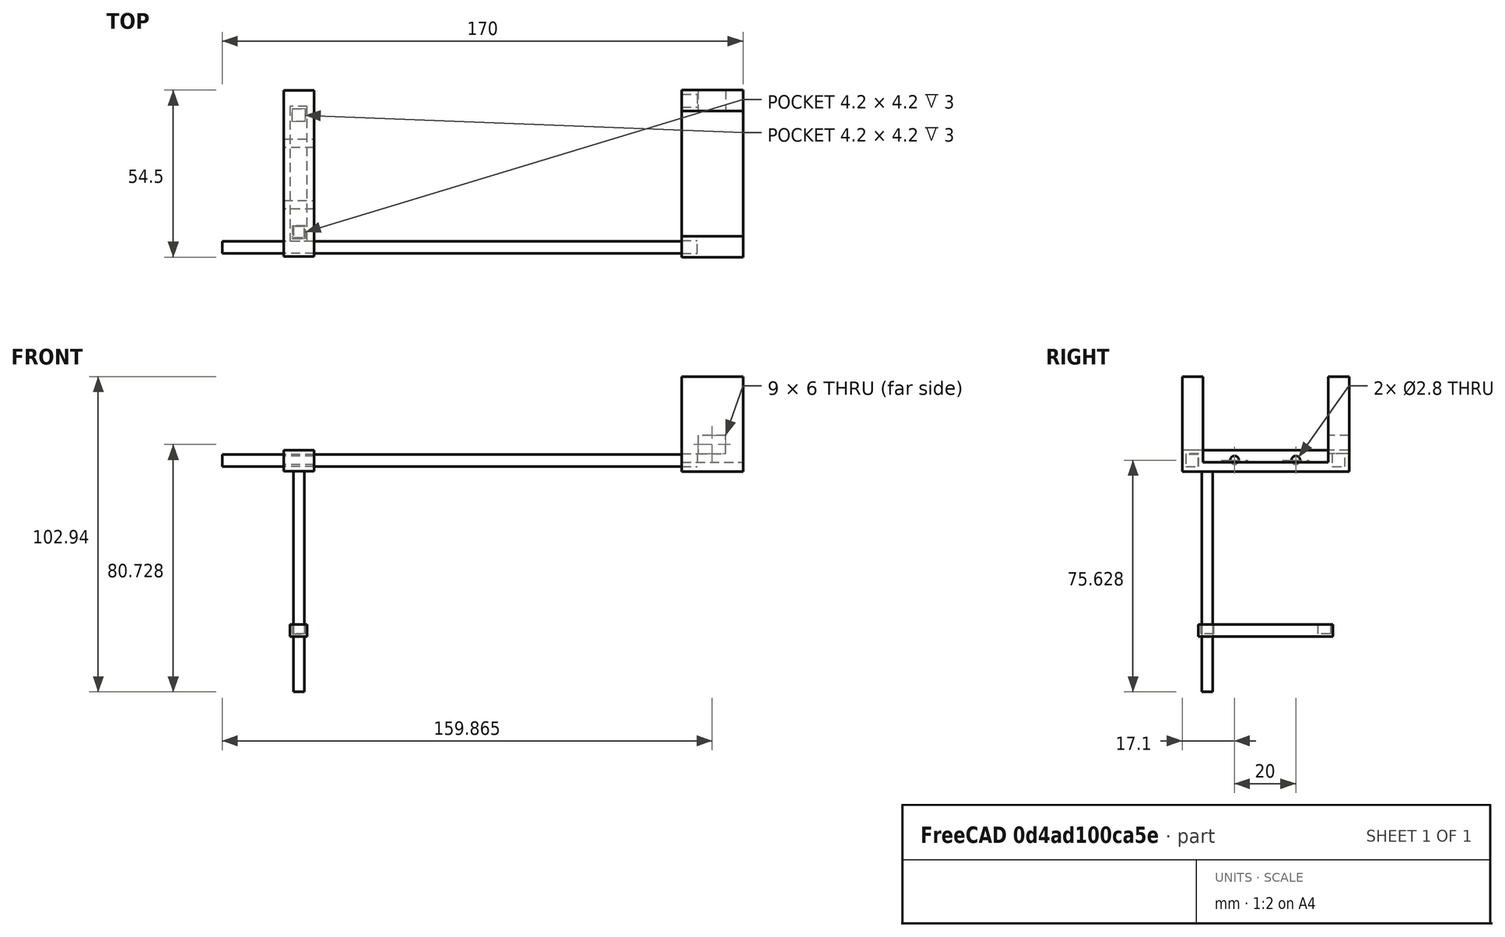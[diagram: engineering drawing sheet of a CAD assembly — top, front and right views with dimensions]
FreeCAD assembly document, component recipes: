
FREECAD ASSEMBLY — COMPONENT RECIPES ("internalstructure")

This assembly document has 7 components, labeled P0..P6 below (a component is one placed body or linked part). 7 of them carry a construction recipe — the FreeCAD feature program that regenerates the part from scratch, quoted from this document or its linked companion documents; the rest are supplied as boundary geometry only. No exploded tour is included for this assembly.
COMPONENT P0 — recipe-attached ("ServoHolderPart001", modeled in this document).
Construction recipe (the document's own serialized feature program — sketch geometry with constraints, then the solid features built on it; lengths are millimeters unless a unit is written):

FEATURE [Sketcher::SketchObject] Sketch  label="ServoHolder"
  FullyConstrained = false
  MapMode = 4
  Placement = pos=(0,0,0) rot=(0.57735,0.57735,0.57735;2.0944rad)
  sketch-geometry (8):
    g0: LineSegment StartX=-27.0989 StartY=-22.5482 StartZ=0 EndX=27.4011 EndY=-22.5482 EndZ=0
    g1: LineSegment StartX=20.6511 StartY=-19.5482 StartZ=0 EndX=20.6511 EndY=8.45178 EndZ=0
    g2: LineSegment StartX=20.6511 StartY=8.45178 StartZ=0 EndX=27.4011 EndY=8.45178 EndZ=0
    g3: LineSegment StartX=-20.3489 StartY=-19.5482 StartZ=0 EndX=-20.3489 EndY=8.45178 EndZ=0
    g4: LineSegment StartX=-20.3489 StartY=8.45178 StartZ=0 EndX=-27.0989 EndY=8.45178 EndZ=0
    g5: LineSegment StartX=20.6511 StartY=-19.5482 StartZ=0 EndX=-20.3489 EndY=-19.5482 EndZ=0
    g6: LineSegment StartX=-27.0989 StartY=8.45178 StartZ=0 EndX=-27.0989 EndY=-22.5482 EndZ=0
    g7: LineSegment StartX=27.4011 StartY=8.45178 StartZ=0 EndX=27.4011 EndY=-22.5482 EndZ=0
  constraints (22):
    c: Horizontal(g0)
    c: Coincident(g1,g2)
    c: Horizontal(g2)
    c: Vertical(g1)
    c: Coincident(g3,g4)
    c: Horizontal(g4)
    c: Vertical(g3)
    c: Coincident(g5,g1)
    c: Coincident(g5,g3)
    c: Horizontal(g5)
    c: Coincident(g6,g4)
    c: Coincident(g6,g0)
    c: Vertical(g6)
    c: Coincident(g7,g2)
    c: Coincident(g7,g0)
    c: Vertical(g7)
    c: DistanceX(g0,g0) = 54.5
    c: DistanceX(g5,g5) = 41
    c: Equal(g4,g2)
    c: Horizontal(g3,g1)
    c: DistanceY(g0,g1) = 3
    c: DistanceY(g1,g1) = 28
FEATURE [PartDesign::Pad] Pad  label="ExtrudeServoHolder"
  Direction = (1,1,1)
  Length = 20
  Length2 = 100
  Placement = pos=(0,0,0) rot=(0.57735,0.57735,0.57735;2.0944rad)
  Profile = -> Sketch
  Type = 0
FEATURE [Sketcher::SketchObject] Sketch001  label="WireHoleSketch"
  FullyConstrained = false
  Placement = pos=(0,27.4011,0) rot=(0,0.707107,0.707107;3.14159rad)
  sketch-geometry (4):
    g0: LineSegment StartX=-5.36505 StartY=-10.7623 StartZ=0 EndX=-14.3651 EndY=-10.7623 EndZ=0
    g1: LineSegment StartX=-14.3651 StartY=-10.7623 StartZ=0 EndX=-14.3651 EndY=-16.7623 EndZ=0
    g2: LineSegment StartX=-14.3651 StartY=-16.7623 StartZ=0 EndX=-5.36505 EndY=-16.7623 EndZ=0
    g3: LineSegment StartX=-5.36505 StartY=-16.7623 StartZ=0 EndX=-5.36505 EndY=-10.7623 EndZ=0
  constraints (10):
    c: Coincident(g1,g2)
    c: Coincident(g2,g3)
    c: Coincident(g3,g0)
    c: Horizontal(g0)
    c: Horizontal(g2)
    c: Vertical(g1)
    c: Vertical(g3)
    c: Coincident(g1,g0)
    c: DistanceX(g0,g0) = 9
    c: DistanceY(g1,g1) = 6
FEATURE [PartDesign::Pocket] Pocket  label="ServoHolder001"
  BaseFeature = -> Pad
  Length = 8
  Length2 = 100
  Placement = pos=(0,0,0) rot=(0.57735,0.57735,0.57735;2.0944rad)
  Profile = -> Sketch001
  Type = 0
FEATURE [Sketcher::SketchObject] Sketch002  label="HorizontalSupportHole"
  FullyConstrained = false
  MapMode = 5
  Placement = pos=(0,0,0) rot=(0.57735,0.57735,-0.57735;4.18879rad)
  Support = -> [Pocket]
  sketch-geometry (8):
    g0: LineSegment StartX=-25.8969 StartY=20.9931 StartZ=0 EndX=-21.6969 EndY=20.9931 EndZ=0
    g1: LineSegment StartX=-21.6969 StartY=20.9931 StartZ=0 EndX=-21.6969 EndY=16.7931 EndZ=0
    g2: LineSegment StartX=-21.6969 StartY=16.7931 StartZ=0 EndX=-25.8969 EndY=16.7931 EndZ=0
    g3: LineSegment StartX=-25.8969 StartY=16.7931 StartZ=0 EndX=-25.8969 EndY=20.9931 EndZ=0
    g4: LineSegment StartX=26.0415 StartY=16.7931 StartZ=0 EndX=21.8415 EndY=16.7931 EndZ=0
    g5: LineSegment StartX=21.8415 StartY=16.7931 StartZ=0 EndX=21.8415 EndY=20.9931 EndZ=0
    g6: LineSegment StartX=21.8415 StartY=20.9931 StartZ=0 EndX=26.0415 EndY=20.9931 EndZ=0
    g7: LineSegment StartX=26.0415 StartY=20.9931 StartZ=0 EndX=26.0415 EndY=16.7931 EndZ=0
  constraints (21):
    c: Coincident(g0,g1)
    c: Coincident(g1,g2)
    c: Coincident(g2,g3)
    c: Coincident(g3,g0)
    c: Horizontal(g0)
    c: Horizontal(g2)
    c: Vertical(g1)
    c: Vertical(g3)
    c: Equal(g0,g1)
    c: DistanceY(g1,g1) = 4.2
    c: Coincident(g4,g5)
    c: Coincident(g5,g6)
    c: Coincident(g6,g7)
    c: Coincident(g7,g4)
    c: Horizontal(g4)
    c: Horizontal(g6)
    c: Vertical(g5)
    c: Vertical(g7)
    c: Equal(g4,g5)
    c: DistanceY(g5,g5) = 4.2  'support_width'
    c: Horizontal(g4,g1)
FEATURE [PartDesign::Pocket] Pocket001  label="SupportPocket"
  BaseFeature = -> Pocket
  Length = 5
  Length2 = 100
  Placement = pos=(0,0,0) rot=(0.57735,0.57735,0.57735;2.0944rad)
  Profile = -> Sketch002
  Type = 0
FEATURE [PartDesign::Body] Body
  Group = -> [Sketch001,Sketch,Pad,Pocket,Sketch002,Pocket001]
  Origin = -> Origin001
  Tip = -> Pocket001
COMPONENT P1 — recipe-attached ("PortConnector4x4x120mm", modeled in this document).
Construction recipe (the document's own serialized feature program — sketch geometry with constraints, then the solid features built on it; lengths are millimeters unless a unit is written):

FEATURE [Sketcher::SketchObject] Sketch003  label="HorizontalSupport001"
  FullyConstrained = false
  Placement = pos=(3e-15,0,0) rot=(0.57735,0.57735,-0.57735;4.18879rad)
  sketch-geometry (4):
    g0: LineSegment StartX=-25.8969 StartY=20.9914 StartZ=0 EndX=-21.8969 EndY=20.9914 EndZ=0
    g1: LineSegment StartX=-21.8969 StartY=20.9914 StartZ=0 EndX=-21.8969 EndY=16.9914 EndZ=0
    g2: LineSegment StartX=-21.8969 StartY=16.9914 StartZ=0 EndX=-25.8969 EndY=16.9914 EndZ=0
    g3: LineSegment StartX=-25.8969 StartY=16.9914 StartZ=0 EndX=-25.8969 EndY=20.9914 EndZ=0
  constraints (10):
    c: Coincident(g0,g1)
    c: Coincident(g1,g2)
    c: Coincident(g2,g3)
    c: Coincident(g3,g0)
    c: Horizontal(g0)
    c: Horizontal(g2)
    c: Vertical(g1)
    c: Vertical(g3)
    c: Equal(g0,g1)
    c: DistanceY(g1,g1) = 4
FEATURE [PartDesign::Pad] Pad001
  Direction = (1,1,1)
  Length = 150
  Length2 = 100
  Placement = pos=(3e-15,0,0) rot=(0.57735,0.57735,-0.57735;4.18879rad)
  Profile = -> Sketch003
  Type = 0
FEATURE [PartDesign::Body] Body001
  Group = -> [Sketch003,Pad001]
  Origin = -> Origin003
  Tip = -> Pad001
COMPONENT P2 — same part as P1; its construction recipe is shown at P1.
COMPONENT P3 — recipe-attached ("Connector4x4x50mm_1", modeled in this document).
Construction recipe (the document's own serialized feature program — sketch geometry with constraints, then the solid features built on it; lengths are millimeters unless a unit is written):

FEATURE [Sketcher::SketchObject] Sketch008
  FullyConstrained = false
  Placement = pos=(-120,-7e-15,-22.4909) rot=(0.707107,-0.707107,0;3.14159rad)
  sketch-geometry (6):
    g0: LineSegment StartX=17.1768 StartY=6.75 StartZ=0 EndX=20.6768 EndY=6.75 EndZ=0
    g1: LineSegment StartX=20.6768 StartY=6.75 StartZ=0 EndX=20.6768 EndY=3.25 EndZ=0
    g2: LineSegment StartX=20.6768 StartY=3.25 StartZ=0 EndX=17.1768 EndY=3.25 EndZ=0
    g3: LineSegment StartX=17.1768 StartY=3.25 StartZ=0 EndX=17.1768 EndY=6.75 EndZ=0
    g4: LineSegment StartX=17.1768 StartY=3.25 StartZ=0 EndX=17.1768 EndY=0 EndZ=0
    g5: LineSegment StartX=17.1768 StartY=6.75 StartZ=0 EndX=17.1768 EndY=10 EndZ=0
  constraints (16):
    c: Coincident(g0,g1)
    c: Coincident(g1,g2)
    c: Coincident(g2,g3)
    c: Coincident(g3,g0)
    c: Horizontal(g0)
    c: Horizontal(g2)
    c: Vertical(g1)
    c: Vertical(g3)
    c: Equal(g0,g1)
    c: DistanceX(g0,g0) = 3.5
    c: Coincident(g4,g2)
    c: PointOnObject(g4,g-1)
    c: Vertical(g4)
    c: Coincident(g5,g0)
    c: Vertical(g5)
    c: Equal(g5,g4)
FEATURE [PartDesign::Pad] Pad003
  Direction = (1,1,1)
  Length = 72
  Length2 = 100
  Placement = pos=(-120,-7e-15,-22.4909) rot=(0.707107,-0.707107,0;3.14159rad)
  Profile = -> Sketch008
  Type = 0
FEATURE [PartDesign::Body] Body003
  Group = -> [Sketch008,Pad003]
  Origin = -> Origin006
  Tip = -> Pad003
COMPONENT P4 — same part as P3; its construction recipe is shown at P3.
COMPONENT P5 — recipe-attached ("BatteryBottomConnector001", modeled in this document).
Construction recipe (the document's own serialized feature program — sketch geometry with constraints, then the solid features built on it; lengths are millimeters unless a unit is written):

FEATURE [Sketcher::SketchObject] Sketch009
  FullyConstrained = false
  Placement = pos=(-120,3.5e-14,-72.4909) rot=(0.707107,-0.707107,0;3.14159rad)
  sketch-geometry (4):
    g0: LineSegment StartX=-22.0524 StartY=7.96105 StartZ=0 EndX=21.7963 EndY=7.96105 EndZ=0
    g1: LineSegment StartX=21.7963 StartY=7.96105 StartZ=0 EndX=21.7963 EndY=2.30544 EndZ=0
    g2: LineSegment StartX=21.7963 StartY=2.30544 StartZ=0 EndX=-22.0524 EndY=2.30544 EndZ=0
    g3: LineSegment StartX=-22.0524 StartY=2.30544 StartZ=0 EndX=-22.0524 EndY=7.96105 EndZ=0
  constraints (8):
    c: Coincident(g0,g1)
    c: Coincident(g1,g2)
    c: Coincident(g2,g3)
    c: Coincident(g3,g0)
    c: Horizontal(g0)
    c: Horizontal(g2)
    c: Vertical(g1)
    c: Vertical(g3)
FEATURE [Sketcher::SketchObject] Sketch010
  FullyConstrained = false
  Placement = pos=(-120,2.3e-14,-72.4909) rot=(0,0,-1;1.5708rad)
  sketch-geometry (8):
    g0: LineSegment StartX=16.8176 StartY=-7.09377 StartZ=0 EndX=21.0176 EndY=-7.09377 EndZ=0
    g1: LineSegment StartX=21.0176 StartY=-7.09377 StartZ=0 EndX=21.0176 EndY=-2.89377 EndZ=0
    g2: LineSegment StartX=21.0176 StartY=-2.89377 StartZ=0 EndX=16.8176 EndY=-2.89377 EndZ=0
    g3: LineSegment StartX=16.8176 StartY=-2.89377 StartZ=0 EndX=16.8176 EndY=-7.09377 EndZ=0
    g4: LineSegment StartX=-17.1303 StartY=-7.13419 StartZ=0 EndX=-21.3303 EndY=-7.13419 EndZ=0
    g5: LineSegment StartX=-21.3303 StartY=-7.13419 StartZ=0 EndX=-21.3303 EndY=-2.93419 EndZ=0
    g6: LineSegment StartX=-21.3303 StartY=-2.93419 StartZ=0 EndX=-17.1303 EndY=-2.93419 EndZ=0
    g7: LineSegment StartX=-17.1303 StartY=-2.93419 StartZ=0 EndX=-17.1303 EndY=-7.13419 EndZ=0
  constraints (20):
    c: Coincident(g0,g1)
    c: Coincident(g1,g2)
    c: Coincident(g2,g3)
    c: Coincident(g3,g0)
    c: Horizontal(g0)
    c: Horizontal(g2)
    c: Vertical(g1)
    c: Vertical(g3)
    c: Equal(g2,g1)
    c: DistanceX(g2,g2) = 4.2
    c: Coincident(g4,g5)
    c: Coincident(g5,g6)
    c: Coincident(g6,g7)
    c: Coincident(g7,g4)
    c: Horizontal(g4)
    c: Horizontal(g6)
    c: Vertical(g5)
    c: Vertical(g7)
    c: Equal(g5,g6)
    c: DistanceX(g6,g6) = 4.2
FEATURE [PartDesign::Pad] Pad004
  Direction = (1,1,1)
  Length = 4
  Length2 = 100
  Placement = pos=(-120,3.5e-14,-72.4909) rot=(0.707107,-0.707107,0;3.14159rad)
  Profile = -> Sketch009
  Type = 0
FEATURE [PartDesign::Pocket] Pocket004
  BaseFeature = -> Pad004
  Length = 3
  Length2 = 100
  Placement = pos=(-120,3.5e-14,-72.4909) rot=(0.707107,-0.707107,0;3.14159rad)
  Profile = -> Sketch010
  Type = 0
FEATURE [PartDesign::Body] Body004
  Group = -> [Sketch009,Sketch010,Pad004,Pocket004]
  Origin = -> Origin009
  Tip = -> Pocket004
COMPONENT P6 — recipe-attached ("BatteryVerticalConnect", modeled in this document).
Construction recipe (the document's own serialized feature program — sketch geometry with constraints, then the solid features built on it; lengths are millimeters unless a unit is written):

FEATURE [Sketcher::SketchObject] Sketch004
  FullyConstrained = false
  Placement = pos=(-120,-2.7e-14,-4e-14) rot=(0.57735,0.57735,-0.57735;4.18879rad)
  sketch-geometry (4):
    g0: LineSegment StartX=-26.9181 StartY=22.4909 StartZ=0 EndX=27.2601 EndY=22.4909 EndZ=0
    g1: LineSegment StartX=27.2601 StartY=22.4909 StartZ=0 EndX=27.2601 EndY=15.6382 EndZ=0
    g2: LineSegment StartX=27.2601 StartY=15.6382 StartZ=0 EndX=-26.9181 EndY=15.6382 EndZ=0
    g3: LineSegment StartX=-26.9181 StartY=15.6382 StartZ=0 EndX=-26.9181 EndY=22.4909 EndZ=0
  constraints (8):
    c: Coincident(g0,g1)
    c: Coincident(g1,g2)
    c: Coincident(g2,g3)
    c: Coincident(g3,g0)
    c: Horizontal(g0)
    c: Horizontal(g2)
    c: Vertical(g1)
    c: Vertical(g3)
FEATURE [PartDesign::Pad] Pad002
  Direction = (1,1,1)
  Length = 10
  Length2 = 100
  Placement = pos=(-120,-2.7e-14,-4e-14) rot=(0.57735,0.57735,-0.57735;4.18879rad)
  Profile = -> Sketch004
  Type = 0
FEATURE [Sketcher::SketchObject] Sketch011
  ExternalGeometry = -> [Pad002]
  FullyConstrained = false
  MapMode = 5
  Placement = pos=(-130,-2.7e-14,-4e-14) rot=(0.57735,0.57735,-0.57735;4.18879rad)
  Support = -> [Pad002]
  sketch-geometry (6):
    g0: Circle CenterX=-10 CenterY=18.8622 CenterZ=0 NormalX=0 NormalY=0 NormalZ=1 AngleXU=0 Radius=1.4
    g1: Circle CenterX=10 CenterY=18.8622 CenterZ=0 NormalX=0 NormalY=0 NormalZ=1 AngleXU=0 Radius=1.4
    g2: LineSegment StartX=10 StartY=18.8622 StartZ=0 EndX=0 EndY=18.8622 EndZ=0
    g3: LineSegment StartX=-10 StartY=18.8622 StartZ=0 EndX=0 EndY=18.8622 EndZ=0
    g4: LineSegment StartX=-26.9181 StartY=18.8622 StartZ=0 EndX=-10 EndY=18.8622 EndZ=0
    g5: LineSegment StartX=10 StartY=18.8622 StartZ=0 EndX=27.2601 EndY=18.8622 EndZ=0
  constraints (16):
    c: Horizontal(g1,g0)
    c: Coincident(g2,g1)
    c: PointOnObject(g2,g-2)
    c: Horizontal(g2)
    c: Coincident(g3,g0)
    c: Coincident(g3,g2)
    c: Equal(g2,g3)
    c: DistanceX(g0,g1) = 20
    c: Equal(g0,g1)
    c: Diameter(g0) = 2.8
    c: PointOnObject(g4,g-4)
    c: Horizontal(g4)
    c: Coincident(g5,g1)
    c: PointOnObject(g5,g-3)
    c: Horizontal(g5)
    c: Coincident(g0,g4)
FEATURE [PartDesign::Pocket] Pocket005
  BaseFeature = -> Pad002
  Length = 25
  Length2 = 100
  Placement = pos=(-120,-2.7e-14,-4e-14) rot=(0.57735,0.57735,-0.57735;4.18879rad)
  Profile = -> Sketch011
  Type = 0
FEATURE [PartDesign::Body] Body002
  Group = -> [Sketch004,Pad002,Sketch011,Pocket005]
  Origin = -> Origin005
  Tip = -> Pocket005
PROVENANCE & LICENSES
A FreeCAD (.FCStd) document from a public repository crawl; recipes are the document's own serialized feature recipes (and, for linked parts, companion documents' recipes).
License: as declared in the source repository (recorded in the dataset sidecar).
